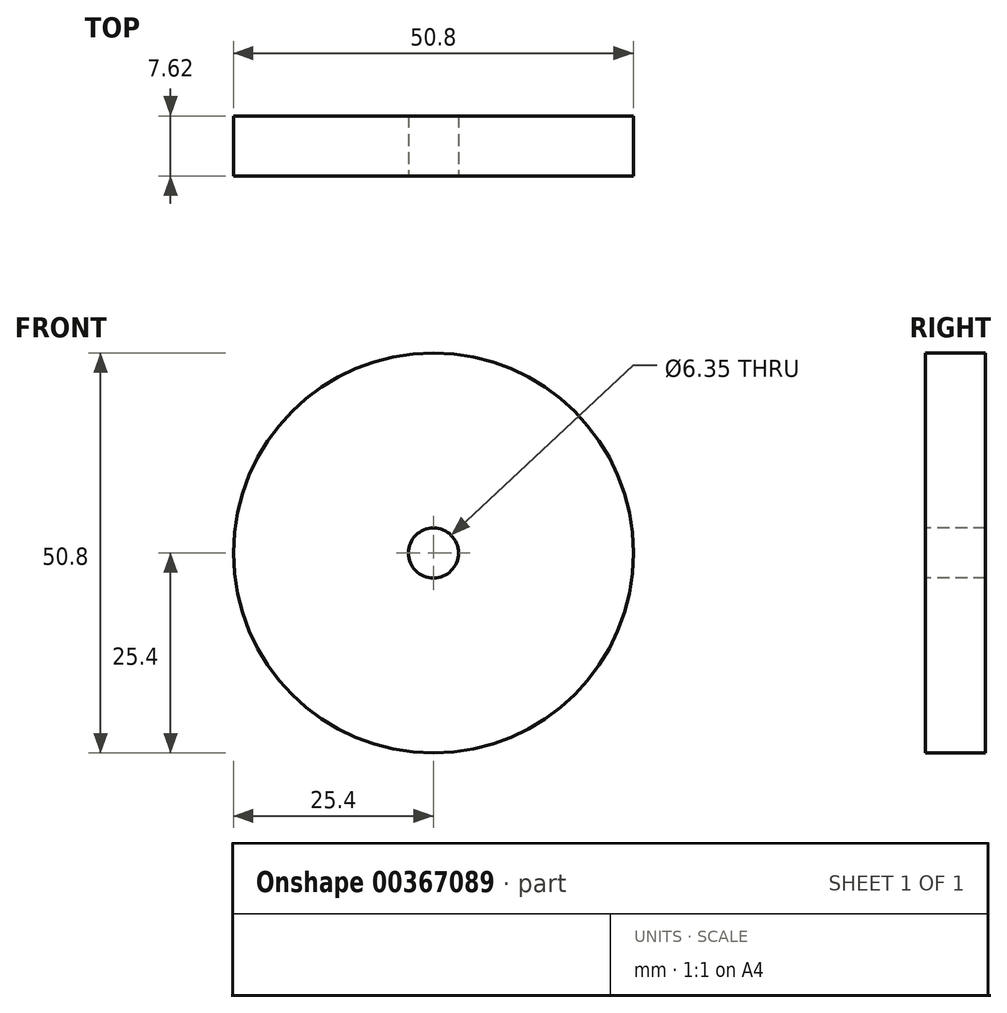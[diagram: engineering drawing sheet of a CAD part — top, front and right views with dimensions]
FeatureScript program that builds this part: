
annotation { "Feature Type Name" : "Feature", "Feature Type Description" : "" }
export const myFeature = defineFeature(function(context is Context, id is Id, definition is map)
    precondition{}
    {
        {
            var Q0;
            Q0=qCreatedBy(makeId("Front.planeOp"),FACE);
            var sketch = newSketch(context, id + "F0", { "sketchPlane" : qUnion([Q0])});
            skCircle(sketch, "E0", {"center": v(0, 0) * mm, "radius": 25.4 * mm});
            skSolve(sketch);
        }
        {
            var Q0;
            Q0=makeQuery(id+"F0.imprint","IMPRINT",FACE,{"disambiguationData":[TD([[makeQuery(id+"F0.imprint","IMPRINT",EDGE,{"derivedFrom":sQuery(id+"F0.wireOp",EDGE,"E0")}),1.0]])]});
            extrude(context, id + "F1", {"entities" : qUnion([Q0]), "depth" : 7.62 * mm});
        }
        {
            var Q0;
            Q0=makeQuery(id+"F1.opExtrude","CAP_FACE",FACE,{"disambiguationData":[OSD([sQuery(id+"F0.wireOp",EDGE,"E0")])],"isStart":false});
            var sketch = newSketch(context, id + "F2", { "sketchPlane" : qUnion([Q0])});
            skPoint(sketch, "E1", {"position": v(0, 0) * mm});
            skSolve(sketch);
        }
        {
            var Q0;
            Q0=sQuery(id+"F2.wireOp",VERTEX,"E1");
            var Q1;
            Q1=makeQuery(id+"F1.opExtrude","SWEPT_BODY",BODY,{"disambiguationData":[OSD([sQuery(id+"F0.wireOp",EDGE,"E0")])]});
            hole(context, id + "F3", {"style" : HoleStyle.SIMPLE, "endStyle" : HoleEndStyle.BLIND, "holeDiameter" : 6.35 * mm, "holeDepth" : 50.8 * mm, "isTappedThrough" : true, "tappedDepth" : 12.7 * mm, "tapClearance" : 3, "locations" : qUnion([Q0]), "scope" : qUnion([Q1])});
        }
    });
